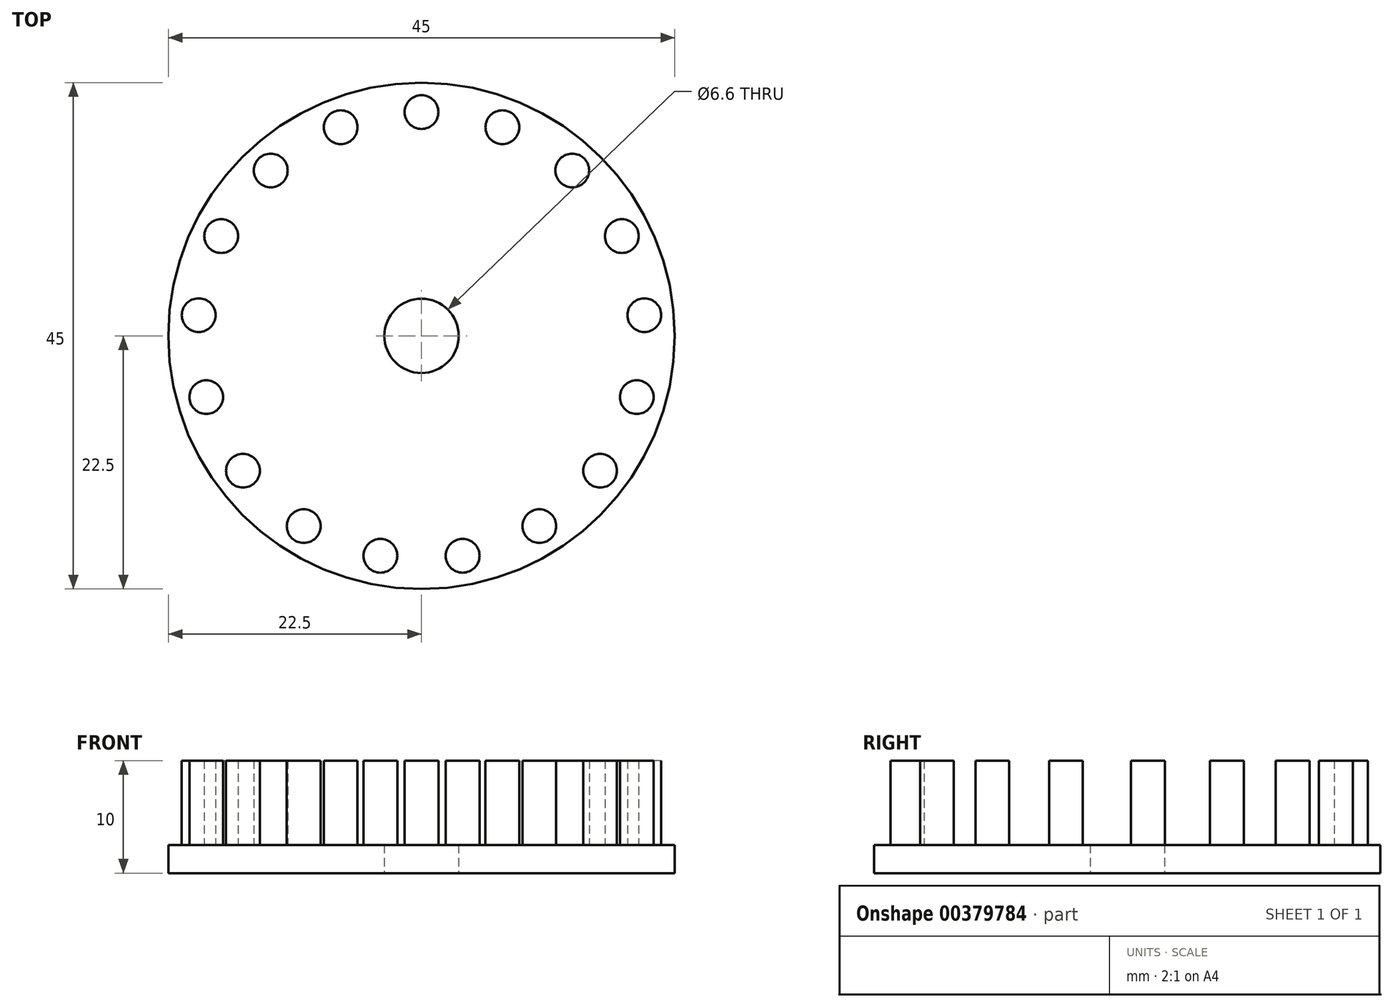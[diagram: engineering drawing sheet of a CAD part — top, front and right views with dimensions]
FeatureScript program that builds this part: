
annotation { "Feature Type Name" : "Feature", "Feature Type Description" : "" }
export const myFeature = defineFeature(function(context is Context, id is Id, definition is map)
    precondition{}
    {
        {
            var Q0;
            Q0=qCreatedBy(makeId("Top.planeOp"),FACE);
            var sketch = newSketch(context, id + "F0", { "sketchPlane" : qUnion([Q0])});
            skCircle(sketch, "E0", {"center": v(0, 0) * mm, "radius": 3.3 * mm});
            skCircle(sketch, "E1", {"center": v(0, 0) * mm, "radius": 22.5 * mm});
            skSolve(sketch);
        }
        {
            var Q0;
            Q0=qSketchRegion(id+"F0",true);
            extrude(context, id + "F1", {"entities" : qUnion([Q0]), "depth" : 2.5 * mm});
        }
        {
            var Q0;
            Q0=makeQuery(id+"F1.opExtrude","CAP_FACE",FACE,{"disambiguationData":[OSD([sQuery(id+"F0.wireOp",EDGE,"E0"),sQuery(id+"F0.wireOp",EDGE,"E1")])],"isStart":false});
            var sketch = newSketch(context, id + "F2", { "sketchPlane" : qUnion([Q0])});
            skCircle(sketch, "E2", {"center": v(0, 19.89) * mm, "radius": 1.5 * mm});
            skCircle(sketch, "E3.1.0", {"center": v(-7.18, 18.54) * mm, "radius": 1.5 * mm});
            skCircle(sketch, "E3.2.0", {"center": v(-13.4, 14.7) * mm, "radius": 1.5 * mm});
            skCircle(sketch, "E3.3.0", {"center": v(-17.8, 8.86) * mm, "radius": 1.5 * mm});
            skCircle(sketch, "E3.4.0", {"center": v(-19.8, 1.83) * mm, "radius": 1.5 * mm});
            skCircle(sketch, "E3.5.0", {"center": v(-19.13, -5.44) * mm, "radius": 1.5 * mm});
            skCircle(sketch, "E3.6.0", {"center": v(-15.87, -11.98) * mm, "radius": 1.5 * mm});
            skCircle(sketch, "E3.7.0", {"center": v(-10.47, -16.9) * mm, "radius": 1.5 * mm});
            skCircle(sketch, "E3.8.0", {"center": v(-3.65, -19.55) * mm, "radius": 1.5 * mm});
            skCircle(sketch, "E3.9.0", {"center": v(3.65, -19.55) * mm, "radius": 1.5 * mm});
            skCircle(sketch, "E3.10.0", {"center": v(10.47, -16.9) * mm, "radius": 1.5 * mm});
            skCircle(sketch, "E3.11.0", {"center": v(15.87, -11.98) * mm, "radius": 1.5 * mm});
            skCircle(sketch, "E3.12.0", {"center": v(19.13, -5.44) * mm, "radius": 1.5 * mm});
            skCircle(sketch, "E3.13.0", {"center": v(19.8, 1.83) * mm, "radius": 1.5 * mm});
            skCircle(sketch, "E3.14.0", {"center": v(17.8, 8.86) * mm, "radius": 1.5 * mm});
            skCircle(sketch, "E3.15.0", {"center": v(13.4, 14.7) * mm, "radius": 1.5 * mm});
            skCircle(sketch, "E3.16.0", {"center": v(7.18, 18.54) * mm, "radius": 1.5 * mm});
            skPoint(sketch, "E3.center", {"position": v(0, 0) * mm});
            skSolve(sketch);
        }
        {
            var Q0;
            Q0=qSketchRegion(id+"F2",true);
            extrude(context, id + "F3", {"entities" : qUnion([Q0]), "operationType" : NewBodyOperationType.ADD, "depth" : 7.5 * mm});
        }
    });
